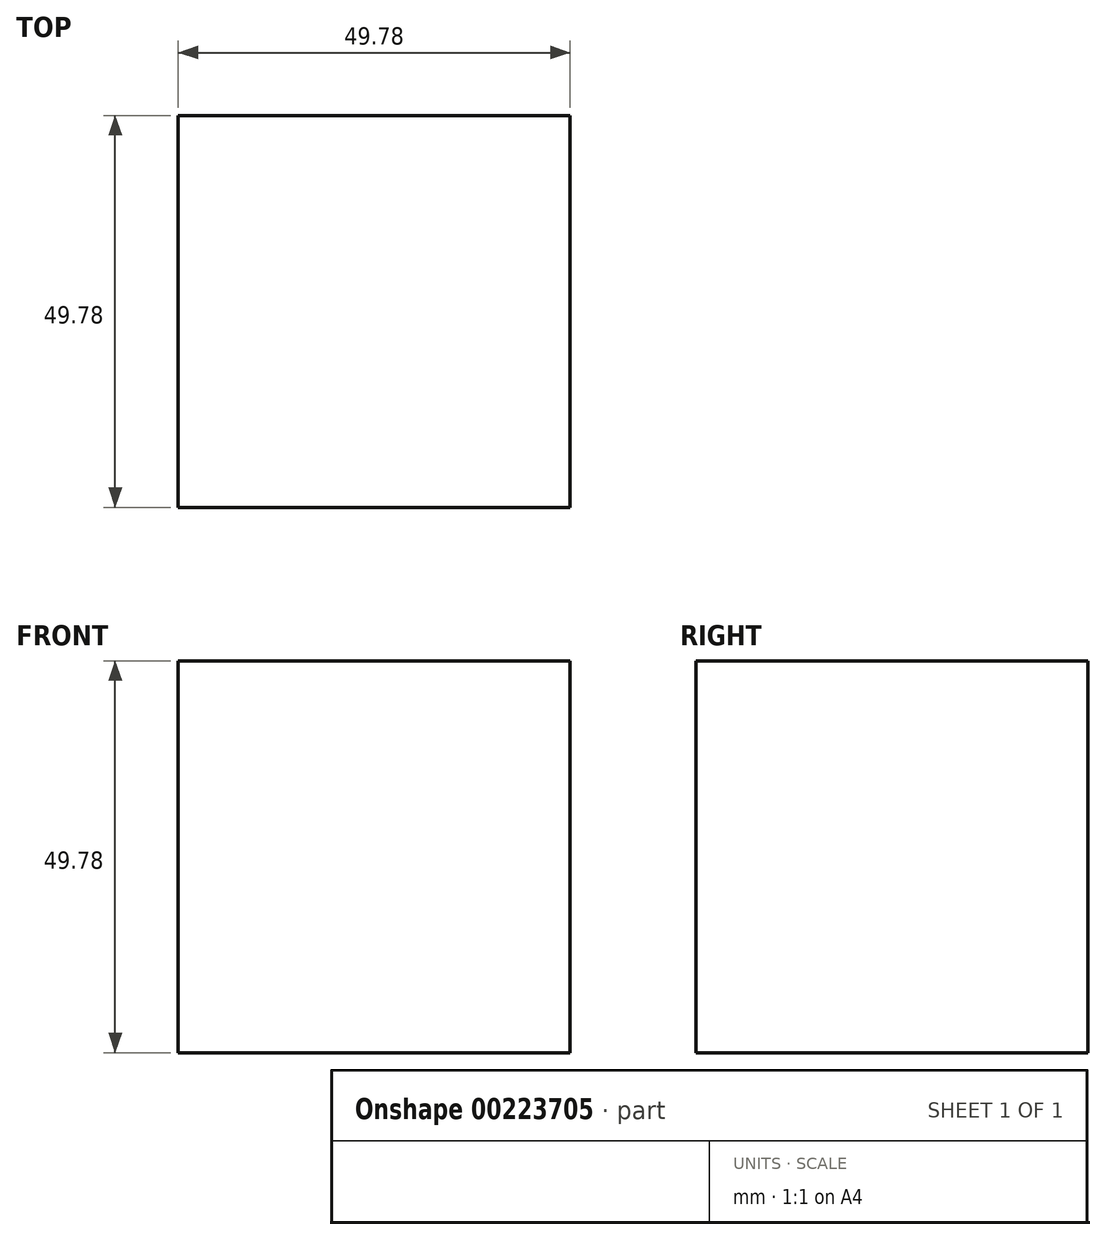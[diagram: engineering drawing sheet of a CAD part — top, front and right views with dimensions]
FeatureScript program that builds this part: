
annotation { "Feature Type Name" : "Feature", "Feature Type Description" : "" }
export const myFeature = defineFeature(function(context is Context, id is Id, definition is map)
    precondition{}
    {
        {
            var Q0;
            Q0=qCreatedBy(makeId("Front.planeOp"),FACE);
            var sketch = newSketch(context, id + "F0", { "sketchPlane" : qUnion([Q0])});
            skLineSegment(sketch, "E0.bottom", {"start": v(-24.9, 24.9) * mm, "end": v(24.9, 24.9) * mm});
            skLineSegment(sketch, "E0.top", {"start": v(-24.9, -24.9) * mm, "end": v(24.9, -24.9) * mm});
            skLineSegment(sketch, "E0.left", {"start": v(-24.9, 24.9) * mm, "end": v(-24.9, -24.9) * mm});
            skLineSegment(sketch, "E0.right", {"start": v(24.9, 24.9) * mm, "end": v(24.9, -24.9) * mm});
            skPoint(sketch, "E0.middle", {"position": v(0, 0) * mm});
            skSolve(sketch);
        }
        {
            var Q0;
            Q0 = qSketchRegion(id + "F0", true);
            extrude(context, id + "F1", {"entities" : qUnion([Q0]), "endBound" : BoundingType.SYMMETRIC, "depth" : 49.78 * mm});
        }
    });
